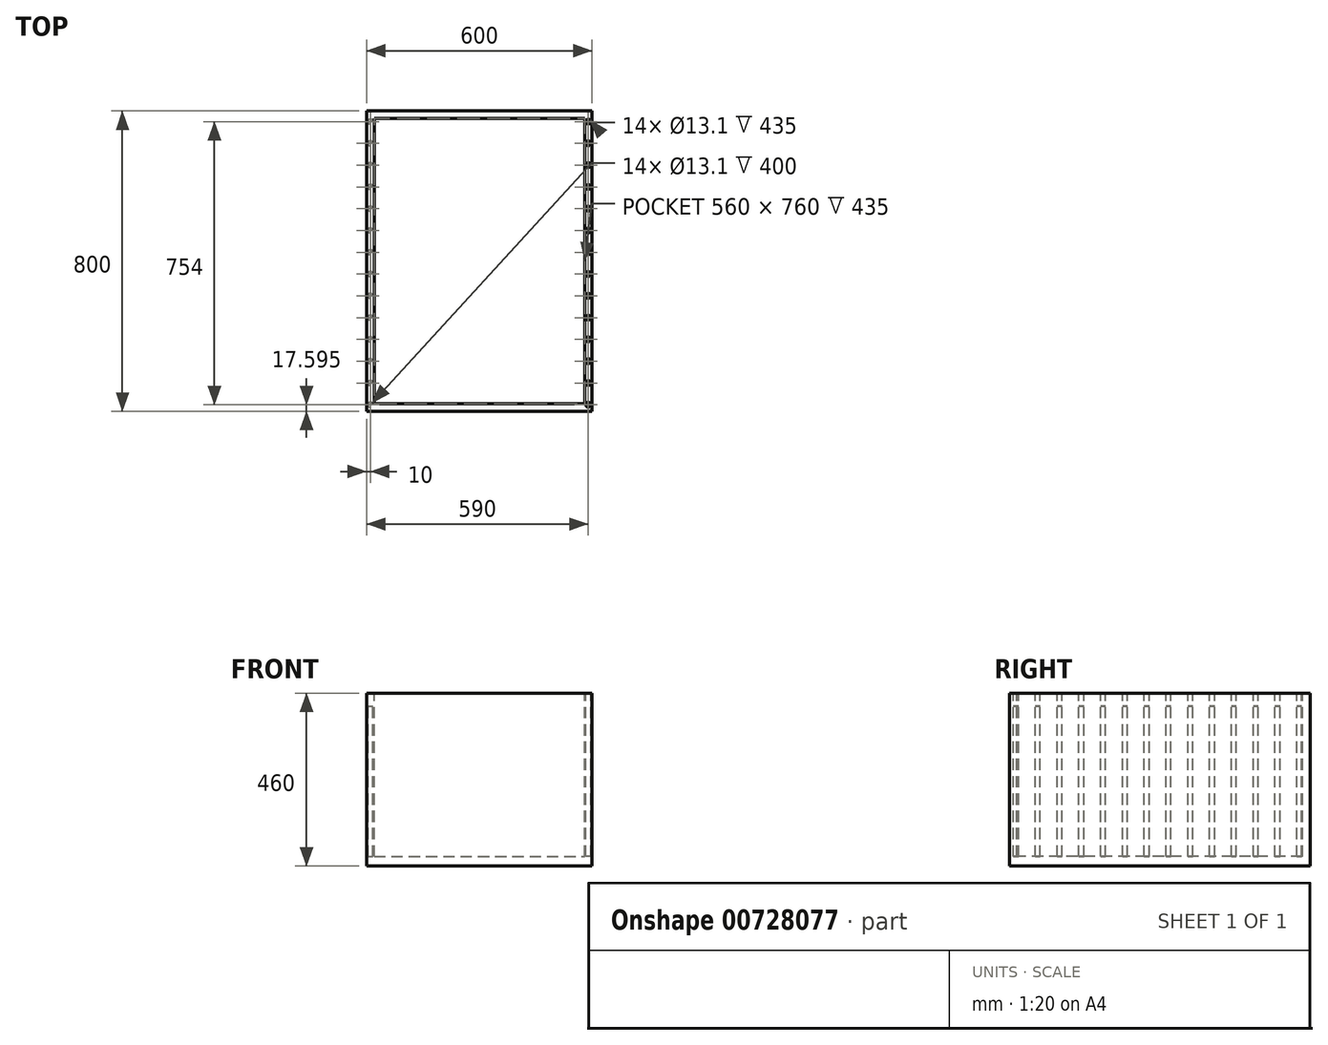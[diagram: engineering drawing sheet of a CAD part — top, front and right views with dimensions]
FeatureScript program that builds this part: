
annotation { "Feature Type Name" : "Feature", "Feature Type Description" : "" }
export const myFeature = defineFeature(function(context is Context, id is Id, definition is map)
    precondition{}
    {
        {
            var Q0;
            Q0=qCreatedBy(makeId("Top.planeOp"),FACE);
            var sketch = newSketch(context, id + "F0", { "sketchPlane" : qUnion([Q0])});
            skLineSegment(sketch, "E0.bottom", {"start": v(-307, 349) * mm, "end": v(293, 349) * mm});
            skLineSegment(sketch, "E0.top", {"start": v(-307, -451) * mm, "end": v(293, -451) * mm});
            skLineSegment(sketch, "E0.left", {"start": v(-307, 349) * mm, "end": v(-307, -451) * mm});
            skLineSegment(sketch, "E0.right", {"start": v(293, 349) * mm, "end": v(293, -451) * mm});
            skLineSegment(sketch, "E1.0", {"start": v(-287, 329) * mm, "end": v(273, 329) * mm});
            skLineSegment(sketch, "E1.1", {"start": v(-287, 329) * mm, "end": v(-287, -431) * mm});
            skLineSegment(sketch, "E1.2", {"start": v(-287, -431) * mm, "end": v(273, -431) * mm});
            skLineSegment(sketch, "E1.3", {"start": v(273, 329) * mm, "end": v(273, -431) * mm});
            skLineSegment(sketch, "E2", {"start": v(-307, -51) * mm, "end": v(-287, -51) * mm, "construction": true});
            skLineSegment(sketch, "E3", {"start": v(-287, -51) * mm, "end": v(-297, -51) * mm, "construction": true});
            skLineSegment(sketch, "E4", {"start": v(-297, -51) * mm, "end": v(-297, -27.4) * mm, "construction": true});
            skCircle(sketch, "E5", {"center": v(-297, -27.4) * mm, "radius": 6.55 * mm});
            skCircle(sketch, "E6.0.1.0", {"center": v(-297, 30.6) * mm, "radius": 6.55 * mm});
            skCircle(sketch, "E6.0.2.0", {"center": v(-297, 88.6) * mm, "radius": 6.55 * mm});
            skCircle(sketch, "E6.0.3.0", {"center": v(-297, 146.6) * mm, "radius": 6.55 * mm});
            skCircle(sketch, "E6.0.4.0", {"center": v(-297, 204.6) * mm, "radius": 6.55 * mm});
            skCircle(sketch, "E6.0.5.0", {"center": v(-297, 262.6) * mm, "radius": 6.55 * mm});
            skCircle(sketch, "E6.0.6.0", {"center": v(-297, 320.6) * mm, "radius": 6.55 * mm});
            skLineSegment(sketch, "E6.direction1", {"start": v(-297, -27.4) * mm, "end": v(-272, -27.4) * mm, "construction": true});
            skLineSegment(sketch, "E6.direction2", {"start": v(-297, -27.4) * mm, "end": v(-297, 30.6) * mm, "construction": true});
            skCircle(sketch, "E7.0.1.0", {"center": v(-297, -85.4) * mm, "radius": 6.55 * mm});
            skCircle(sketch, "E7.0.2.0", {"center": v(-297, -143.4) * mm, "radius": 6.55 * mm});
            skCircle(sketch, "E7.0.3.0", {"center": v(-297, -201.4) * mm, "radius": 6.55 * mm});
            skCircle(sketch, "E7.0.4.0", {"center": v(-297, -259.4) * mm, "radius": 6.55 * mm});
            skCircle(sketch, "E7.0.5.0", {"center": v(-297, -317.4) * mm, "radius": 6.55 * mm});
            skCircle(sketch, "E7.0.6.0", {"center": v(-297, -375.4) * mm, "radius": 6.55 * mm});
            skCircle(sketch, "E7.0.7.0", {"center": v(-297, -433.4) * mm, "radius": 6.55 * mm});
            skLineSegment(sketch, "E7.direction1", {"start": v(-297, -27.4) * mm, "end": v(-257, -27.4) * mm, "construction": true});
            skLineSegment(sketch, "E7.direction2", {"start": v(-297, -27.4) * mm, "end": v(-297, -85.4) * mm, "construction": true});
            skLineSegment(sketch, "E8", {"start": v(-7, 329) * mm, "end": v(-7, -431) * mm, "construction": true});
            skCircle(sketch, "E9.MirrorC", {"center": v(283, 320.6) * mm, "radius": 6.55 * mm});
            skCircle(sketch, "E10.MirrorC", {"center": v(283, 262.6) * mm, "radius": 6.55 * mm});
            skCircle(sketch, "E11.MirrorC", {"center": v(283, 204.6) * mm, "radius": 6.55 * mm});
            skCircle(sketch, "E12.MirrorC", {"center": v(283, 146.6) * mm, "radius": 6.55 * mm});
            skCircle(sketch, "E13.MirrorC", {"center": v(283, 88.6) * mm, "radius": 6.55 * mm});
            skCircle(sketch, "E14.MirrorC", {"center": v(283, 30.6) * mm, "radius": 6.55 * mm});
            skCircle(sketch, "E15.MirrorC", {"center": v(283, -27.4) * mm, "radius": 6.55 * mm});
            skCircle(sketch, "E16.MirrorC", {"center": v(283, -85.4) * mm, "radius": 6.55 * mm});
            skCircle(sketch, "E17.MirrorC", {"center": v(283, -143.4) * mm, "radius": 6.55 * mm});
            skCircle(sketch, "E18.MirrorC", {"center": v(283, -201.4) * mm, "radius": 6.55 * mm});
            skCircle(sketch, "E19.MirrorC", {"center": v(283, -259.4) * mm, "radius": 6.55 * mm});
            skCircle(sketch, "E20.MirrorC", {"center": v(283, -317.4) * mm, "radius": 6.55 * mm});
            skCircle(sketch, "E21.MirrorC", {"center": v(283, -375.4) * mm, "radius": 6.55 * mm});
            skCircle(sketch, "E22.MirrorC", {"center": v(283, -433.4) * mm, "radius": 6.55 * mm});
            skSolve(sketch);
        }
        {
            var Q0;
            Q0=makeQuery(id+"F0.imprint","IMPRINT",FACE,{"disambiguationData":[TD([[makeQuery(id+"F0.imprint","IMPRINT",EDGE,{"derivedFrom":sQuery(id+"F0.wireOp",EDGE,"E0.bottom")}),-1.0]])]});
            var Q1;
            Q1=makeQuery(id+"F0.imprint","IMPRINT",FACE,{"disambiguationData":[TD([[makeQuery(id+"F0.imprint","IMPRINT",EDGE,{"derivedFrom":sQuery(id+"F0.wireOp",EDGE,"E22.MirrorC")}),-1.0]])]});
            var Q2;
            Q2=makeQuery(id+"F0.imprint","IMPRINT",FACE,{"disambiguationData":[TD([[makeQuery(id+"F0.imprint","IMPRINT",EDGE,{"derivedFrom":sQuery(id+"F0.wireOp",EDGE,"E21.MirrorC")}),-1.0]])]});
            var Q3;
            Q3=makeQuery(id+"F0.imprint","IMPRINT",FACE,{"disambiguationData":[TD([[makeQuery(id+"F0.imprint","IMPRINT",EDGE,{"derivedFrom":sQuery(id+"F0.wireOp",EDGE,"E20.MirrorC")}),-1.0]])]});
            var Q4;
            Q4=makeQuery(id+"F0.imprint","IMPRINT",FACE,{"disambiguationData":[TD([[makeQuery(id+"F0.imprint","IMPRINT",EDGE,{"derivedFrom":sQuery(id+"F0.wireOp",EDGE,"E19.MirrorC")}),-1.0]])]});
            var Q5;
            Q5=makeQuery(id+"F0.imprint","IMPRINT",FACE,{"disambiguationData":[TD([[makeQuery(id+"F0.imprint","IMPRINT",EDGE,{"derivedFrom":sQuery(id+"F0.wireOp",EDGE,"E18.MirrorC")}),-1.0]])]});
            var Q6;
            Q6=makeQuery(id+"F0.imprint","IMPRINT",FACE,{"disambiguationData":[TD([[makeQuery(id+"F0.imprint","IMPRINT",EDGE,{"derivedFrom":sQuery(id+"F0.wireOp",EDGE,"E17.MirrorC")}),-1.0]])]});
            var Q7;
            Q7=makeQuery(id+"F0.imprint","IMPRINT",FACE,{"disambiguationData":[TD([[makeQuery(id+"F0.imprint","IMPRINT",EDGE,{"derivedFrom":sQuery(id+"F0.wireOp",EDGE,"E16.MirrorC")}),-1.0]])]});
            var Q8;
            Q8=makeQuery(id+"F0.imprint","IMPRINT",FACE,{"disambiguationData":[TD([[makeQuery(id+"F0.imprint","IMPRINT",EDGE,{"derivedFrom":sQuery(id+"F0.wireOp",EDGE,"E15.MirrorC")}),-1.0]])]});
            var Q9;
            Q9=makeQuery(id+"F0.imprint","IMPRINT",FACE,{"disambiguationData":[TD([[makeQuery(id+"F0.imprint","IMPRINT",EDGE,{"derivedFrom":sQuery(id+"F0.wireOp",EDGE,"E14.MirrorC")}),-1.0]])]});
            var Q10;
            Q10=makeQuery(id+"F0.imprint","IMPRINT",FACE,{"disambiguationData":[TD([[makeQuery(id+"F0.imprint","IMPRINT",EDGE,{"derivedFrom":sQuery(id+"F0.wireOp",EDGE,"E13.MirrorC")}),-1.0]])]});
            var Q11;
            Q11=makeQuery(id+"F0.imprint","IMPRINT",FACE,{"disambiguationData":[TD([[makeQuery(id+"F0.imprint","IMPRINT",EDGE,{"derivedFrom":sQuery(id+"F0.wireOp",EDGE,"E12.MirrorC")}),-1.0]])]});
            var Q12;
            Q12=makeQuery(id+"F0.imprint","IMPRINT",FACE,{"disambiguationData":[TD([[makeQuery(id+"F0.imprint","IMPRINT",EDGE,{"derivedFrom":sQuery(id+"F0.wireOp",EDGE,"E11.MirrorC")}),-1.0]])]});
            var Q13;
            Q13=makeQuery(id+"F0.imprint","IMPRINT",FACE,{"disambiguationData":[TD([[makeQuery(id+"F0.imprint","IMPRINT",EDGE,{"derivedFrom":sQuery(id+"F0.wireOp",EDGE,"E10.MirrorC")}),-1.0]])]});
            var Q14;
            Q14=makeQuery(id+"F0.imprint","IMPRINT",FACE,{"disambiguationData":[TD([[makeQuery(id+"F0.imprint","IMPRINT",EDGE,{"derivedFrom":sQuery(id+"F0.wireOp",EDGE,"E9.MirrorC")}),-1.0]])]});
            var Q15;
            Q15=makeQuery(id+"F0.imprint","IMPRINT",FACE,{"disambiguationData":[TD([[makeQuery(id+"F0.imprint","IMPRINT",EDGE,{"derivedFrom":sQuery(id+"F0.wireOp",EDGE,"E6.0.6.0")}),1.0]])]});
            var Q16;
            Q16=makeQuery(id+"F0.imprint","IMPRINT",FACE,{"disambiguationData":[TD([[makeQuery(id+"F0.imprint","IMPRINT",EDGE,{"derivedFrom":sQuery(id+"F0.wireOp",EDGE,"E6.0.5.0")}),1.0]])]});
            var Q17;
            Q17=makeQuery(id+"F0.imprint","IMPRINT",FACE,{"disambiguationData":[TD([[makeQuery(id+"F0.imprint","IMPRINT",EDGE,{"derivedFrom":sQuery(id+"F0.wireOp",EDGE,"E6.0.4.0")}),1.0]])]});
            var Q18;
            Q18=makeQuery(id+"F0.imprint","IMPRINT",FACE,{"disambiguationData":[TD([[makeQuery(id+"F0.imprint","IMPRINT",EDGE,{"derivedFrom":sQuery(id+"F0.wireOp",EDGE,"E6.0.3.0")}),1.0]])]});
            var Q19;
            Q19=makeQuery(id+"F0.imprint","IMPRINT",FACE,{"disambiguationData":[TD([[makeQuery(id+"F0.imprint","IMPRINT",EDGE,{"derivedFrom":sQuery(id+"F0.wireOp",EDGE,"E6.0.2.0")}),1.0]])]});
            var Q20;
            Q20=makeQuery(id+"F0.imprint","IMPRINT",FACE,{"disambiguationData":[TD([[makeQuery(id+"F0.imprint","IMPRINT",EDGE,{"derivedFrom":sQuery(id+"F0.wireOp",EDGE,"E6.0.1.0")}),1.0]])]});
            var Q21;
            Q21=makeQuery(id+"F0.imprint","IMPRINT",FACE,{"disambiguationData":[TD([[makeQuery(id+"F0.imprint","IMPRINT",EDGE,{"derivedFrom":sQuery(id+"F0.wireOp",EDGE,"E5")}),1.0]])]});
            var Q22;
            Q22=makeQuery(id+"F0.imprint","IMPRINT",FACE,{"disambiguationData":[TD([[makeQuery(id+"F0.imprint","IMPRINT",EDGE,{"derivedFrom":sQuery(id+"F0.wireOp",EDGE,"E7.0.1.0")}),1.0]])]});
            var Q23;
            Q23=makeQuery(id+"F0.imprint","IMPRINT",FACE,{"disambiguationData":[TD([[makeQuery(id+"F0.imprint","IMPRINT",EDGE,{"derivedFrom":sQuery(id+"F0.wireOp",EDGE,"E7.0.2.0")}),1.0]])]});
            var Q24;
            Q24=makeQuery(id+"F0.imprint","IMPRINT",FACE,{"disambiguationData":[TD([[makeQuery(id+"F0.imprint","IMPRINT",EDGE,{"derivedFrom":sQuery(id+"F0.wireOp",EDGE,"E7.0.3.0")}),1.0]])]});
            var Q25;
            Q25=makeQuery(id+"F0.imprint","IMPRINT",FACE,{"disambiguationData":[TD([[makeQuery(id+"F0.imprint","IMPRINT",EDGE,{"derivedFrom":sQuery(id+"F0.wireOp",EDGE,"E7.0.4.0")}),1.0]])]});
            var Q26;
            Q26=makeQuery(id+"F0.imprint","IMPRINT",FACE,{"disambiguationData":[TD([[makeQuery(id+"F0.imprint","IMPRINT",EDGE,{"derivedFrom":sQuery(id+"F0.wireOp",EDGE,"E7.0.5.0")}),1.0]])]});
            var Q27;
            Q27=makeQuery(id+"F0.imprint","IMPRINT",FACE,{"disambiguationData":[TD([[makeQuery(id+"F0.imprint","IMPRINT",EDGE,{"derivedFrom":sQuery(id+"F0.wireOp",EDGE,"E7.0.6.0")}),1.0]])]});
            var Q28;
            Q28=makeQuery(id+"F0.imprint","IMPRINT",FACE,{"disambiguationData":[TD([[makeQuery(id+"F0.imprint","IMPRINT",EDGE,{"derivedFrom":sQuery(id+"F0.wireOp",EDGE,"E7.0.7.0")}),1.0]])]});
            extrude(context, id + "F1", {"entities" : qUnion([Q0, Q1, Q2, Q3, Q4, Q5, Q6, Q7, Q8, Q9, Q10, Q11, Q12, Q13, Q14, Q15, Q16, Q17, Q18, Q19, Q20, Q21, Q22, Q23, Q24, Q25, Q26, Q27, Q28]), "oppositeDirection" : true, "depth" : 35 * mm});
        }
        {
            var Q0;
            Q0=makeQuery(id+"F1.opExtrude","CAP_FACE",FACE,{"disambiguationData":[OSD([sQuery(id+"F0.wireOp",EDGE,"E0.bottom"),sQuery(id+"F0.wireOp",EDGE,"E0.top"),sQuery(id+"F0.wireOp",EDGE,"E0.left"),sQuery(id+"F0.wireOp",EDGE,"E0.right"),sQuery(id+"F0.wireOp",EDGE,"E1.0"),sQuery(id+"F0.wireOp",EDGE,"E1.1"),sQuery(id+"F0.wireOp",EDGE,"E1.2"),sQuery(id+"F0.wireOp",EDGE,"E1.3")])],"isStart":false});
            var sketch = newSketch(context, id + "F2", { "sketchPlane" : qUnion([Q0])});
            skCircle(sketch, "E23.0", {"center": v(283, 85.4) * mm, "radius": 6.55 * mm});
            skCircle(sketch, "E23.1", {"center": v(283, -320.6) * mm, "radius": 6.55 * mm});
            skCircle(sketch, "E23.2", {"center": v(283, -204.6) * mm, "radius": 6.55 * mm});
            skCircle(sketch, "E23.3", {"center": v(283, -262.6) * mm, "radius": 6.55 * mm});
            skCircle(sketch, "E23.4", {"center": v(283, 143.4) * mm, "radius": 6.55 * mm});
            skCircle(sketch, "E23.5", {"center": v(283, 259.4) * mm, "radius": 6.55 * mm});
            skCircle(sketch, "E23.6", {"center": v(283, -146.6) * mm, "radius": 6.55 * mm});
            skCircle(sketch, "E23.7", {"center": v(283, 317.4) * mm, "radius": 6.55 * mm});
            skCircle(sketch, "E23.8", {"center": v(283, 201.4) * mm, "radius": 6.55 * mm});
            skCircle(sketch, "E23.9", {"center": v(283, -30.6) * mm, "radius": 6.55 * mm});
            skCircle(sketch, "E23.10", {"center": v(283, 27.4) * mm, "radius": 6.55 * mm});
            skCircle(sketch, "E23.11", {"center": v(283, 433.4) * mm, "radius": 6.55 * mm});
            skCircle(sketch, "E23.12", {"center": v(283, 375.4) * mm, "radius": 6.55 * mm});
            skCircle(sketch, "E23.13", {"center": v(283, -88.6) * mm, "radius": 6.55 * mm});
            skCircle(sketch, "E24.0", {"center": v(-297, -30.6) * mm, "radius": 6.55 * mm});
            skCircle(sketch, "E24.1", {"center": v(-297, 259.4) * mm, "radius": 6.55 * mm});
            skCircle(sketch, "E24.2", {"center": v(-297, -320.6) * mm, "radius": 6.55 * mm});
            skLineSegment(sketch, "E24.3", {"start": v(-297, 51) * mm, "end": v(-297, 27.4) * mm});
            skCircle(sketch, "E24.4", {"center": v(-297, -204.6) * mm, "radius": 6.55 * mm});
            skCircle(sketch, "E24.5", {"center": v(-297, -146.6) * mm, "radius": 6.55 * mm});
            skCircle(sketch, "E24.6", {"center": v(-297, 201.4) * mm, "radius": 6.55 * mm});
            skCircle(sketch, "E24.7", {"center": v(-297, 317.4) * mm, "radius": 6.55 * mm});
            skCircle(sketch, "E24.8", {"center": v(-297, 375.4) * mm, "radius": 6.55 * mm});
            skCircle(sketch, "E24.9", {"center": v(-297, -88.6) * mm, "radius": 6.55 * mm});
            skCircle(sketch, "E24.10", {"center": v(-297, 143.4) * mm, "radius": 6.55 * mm});
            skCircle(sketch, "E24.11", {"center": v(-297, 27.4) * mm, "radius": 6.55 * mm});
            skLineSegment(sketch, "E24.12", {"start": v(-297, 27.4) * mm, "end": v(-297, 85.4) * mm});
            skCircle(sketch, "E24.13", {"center": v(-297, -262.6) * mm, "radius": 6.55 * mm});
            skCircle(sketch, "E24.14", {"center": v(-297, 85.4) * mm, "radius": 6.55 * mm});
            skLineSegment(sketch, "E24.15", {"start": v(-297, 27.4) * mm, "end": v(-297, -30.6) * mm});
            skCircle(sketch, "E24.16", {"center": v(-297, 433.4) * mm, "radius": 6.55 * mm});
            skSolve(sketch);
        }
        {
            var Q0;
            Q0=makeQuery(id+"F2.imprint","IMPRINT",FACE,{"disambiguationData":[TD([[makeQuery(id+"F2.imprint","IMPRINT",EDGE,{"derivedFrom":sQuery(id+"F2.wireOp",EDGE,"E24.16")}),-1.0]])]});
            var Q1;
            Q1=makeQuery(id+"F2.imprint","IMPRINT",FACE,{"disambiguationData":[TD([[makeQuery(id+"F2.imprint","IMPRINT",EDGE,{"derivedFrom":sQuery(id+"F2.wireOp",EDGE,"E24.10")}),-1.0]])]});
            var Q2;
            Q2=makeQuery(id+"F2.imprint","IMPRINT",FACE,{"disambiguationData":[TD([[makeQuery(id+"F2.imprint","IMPRINT",EDGE,{"derivedFrom":sQuery(id+"F2.wireOp",EDGE,"E24.8")}),-1.0]])]});
            var Q3;
            Q3=makeQuery(id+"F2.imprint","IMPRINT",FACE,{"disambiguationData":[TD([[makeQuery(id+"F2.imprint","IMPRINT",EDGE,{"derivedFrom":sQuery(id+"F2.wireOp",EDGE,"E24.4")}),-1.0]])]});
            var Q4;
            {var subQ0=sQuery(id+"F2.wireOp",EDGE,"E24.12");var subQ1=sQuery(id+"F2.wireOp",EDGE,"E24.11");var subQ2=makeQuery(id+"F2.imprint","INTERSECT",VERTEX,{"derivedFrom":[subQ1,subQ0]});Q4=makeQuery(id+"F2.imprint","IMPRINT",FACE,{"disambiguationData":[TD([[makeQuery(id+"F2.imprint","IMPRINT",EDGE,{"disambiguationData":[TD([[subQ2,-1.0]])],"derivedFrom":subQ1}),-1.0]])]});}
            var Q5;
            Q5=makeQuery(id+"F2.imprint","IMPRINT",FACE,{"disambiguationData":[TD([[makeQuery(id+"F2.imprint","IMPRINT",EDGE,{"derivedFrom":sQuery(id+"F2.wireOp",EDGE,"E24.13")}),-1.0]])]});
            var Q6;
            Q6=makeQuery(id+"F2.imprint","IMPRINT",FACE,{"disambiguationData":[TD([[makeQuery(id+"F2.imprint","IMPRINT",EDGE,{"derivedFrom":sQuery(id+"F2.wireOp",EDGE,"E24.5")}),-1.0]])]});
            var Q7;
            Q7=makeQuery(id+"F2.imprint","IMPRINT",FACE,{"disambiguationData":[TD([[makeQuery(id+"F2.imprint","IMPRINT",EDGE,{"derivedFrom":sQuery(id+"F2.wireOp",EDGE,"E24.1")}),-1.0]])]});
            var Q8;
            Q8=makeQuery(id+"F2.imprint","IMPRINT",FACE,{"disambiguationData":[TD([[makeQuery(id+"F2.imprint","IMPRINT",EDGE,{"derivedFrom":sQuery(id+"F2.wireOp",EDGE,"E23.13")}),1.0]])]});
            var Q9;
            Q9=makeQuery(id+"F2.imprint","IMPRINT",FACE,{"disambiguationData":[TD([[makeQuery(id+"F2.imprint","IMPRINT",EDGE,{"derivedFrom":sQuery(id+"F2.wireOp",EDGE,"E24.0")}),-1.0]])]});
            var Q10;
            Q10=makeQuery(id+"F2.imprint","IMPRINT",FACE,{"disambiguationData":[TD([[makeQuery(id+"F2.imprint","IMPRINT",EDGE,{"derivedFrom":sQuery(id+"F2.wireOp",EDGE,"E23.0")}),1.0]])]});
            var Q11;
            Q11=makeQuery(id+"F2.imprint","IMPRINT",FACE,{"disambiguationData":[TD([[makeQuery(id+"F2.imprint","IMPRINT",EDGE,{"derivedFrom":sQuery(id+"F2.wireOp",EDGE,"E23.1")}),1.0]])]});
            var Q12;
            Q12=makeQuery(id+"F2.imprint","IMPRINT",FACE,{"disambiguationData":[TD([[makeQuery(id+"F2.imprint","IMPRINT",EDGE,{"derivedFrom":sQuery(id+"F2.wireOp",EDGE,"E23.2")}),1.0]])]});
            var Q13;
            Q13=makeQuery(id+"F2.imprint","IMPRINT",FACE,{"disambiguationData":[TD([[makeQuery(id+"F2.imprint","IMPRINT",EDGE,{"derivedFrom":sQuery(id+"F2.wireOp",EDGE,"E23.3")}),1.0]])]});
            var Q14;
            Q14=makeQuery(id+"F2.imprint","IMPRINT",FACE,{"disambiguationData":[TD([[makeQuery(id+"F2.imprint","IMPRINT",EDGE,{"derivedFrom":sQuery(id+"F2.wireOp",EDGE,"E23.4")}),1.0]])]});
            var Q15;
            Q15=makeQuery(id+"F2.imprint","IMPRINT",FACE,{"disambiguationData":[TD([[makeQuery(id+"F2.imprint","IMPRINT",EDGE,{"derivedFrom":sQuery(id+"F2.wireOp",EDGE,"E23.5")}),1.0]])]});
            var Q16;
            Q16=makeQuery(id+"F2.imprint","IMPRINT",FACE,{"disambiguationData":[TD([[makeQuery(id+"F2.imprint","IMPRINT",EDGE,{"derivedFrom":sQuery(id+"F2.wireOp",EDGE,"E23.6")}),1.0]])]});
            var Q17;
            Q17=makeQuery(id+"F2.imprint","IMPRINT",FACE,{"disambiguationData":[TD([[makeQuery(id+"F2.imprint","IMPRINT",EDGE,{"derivedFrom":sQuery(id+"F2.wireOp",EDGE,"E23.7")}),1.0]])]});
            var Q18;
            Q18=makeQuery(id+"F2.imprint","IMPRINT",FACE,{"disambiguationData":[TD([[makeQuery(id+"F2.imprint","IMPRINT",EDGE,{"derivedFrom":sQuery(id+"F2.wireOp",EDGE,"E23.8")}),1.0]])]});
            var Q19;
            Q19=makeQuery(id+"F2.imprint","IMPRINT",FACE,{"disambiguationData":[TD([[makeQuery(id+"F2.imprint","IMPRINT",EDGE,{"derivedFrom":sQuery(id+"F2.wireOp",EDGE,"E23.9")}),1.0]])]});
            var Q20;
            Q20=makeQuery(id+"F2.imprint","IMPRINT",FACE,{"disambiguationData":[TD([[makeQuery(id+"F2.imprint","IMPRINT",EDGE,{"derivedFrom":sQuery(id+"F2.wireOp",EDGE,"E23.10")}),1.0]])]});
            var Q21;
            Q21=makeQuery(id+"F2.imprint","IMPRINT",FACE,{"disambiguationData":[TD([[makeQuery(id+"F2.imprint","IMPRINT",EDGE,{"derivedFrom":sQuery(id+"F2.wireOp",EDGE,"E24.14")}),-1.0]])]});
            var Q22;
            Q22=makeQuery(id+"F2.imprint","IMPRINT",FACE,{"disambiguationData":[TD([[makeQuery(id+"F2.imprint","IMPRINT",EDGE,{"derivedFrom":sQuery(id+"F2.wireOp",EDGE,"E24.6")}),-1.0]])]});
            var Q23;
            Q23=makeQuery(id+"F2.imprint","IMPRINT",FACE,{"disambiguationData":[TD([[makeQuery(id+"F2.imprint","IMPRINT",EDGE,{"derivedFrom":sQuery(id+"F2.wireOp",EDGE,"E24.9")}),-1.0]])]});
            var Q24;
            Q24=makeQuery(id+"F2.imprint","IMPRINT",FACE,{"disambiguationData":[TD([[makeQuery(id+"F2.imprint","IMPRINT",EDGE,{"derivedFrom":sQuery(id+"F2.wireOp",EDGE,"E24.7")}),-1.0]])]});
            var Q25;
            Q25=makeQuery(id+"F2.imprint","IMPRINT",FACE,{"disambiguationData":[TD([[makeQuery(id+"F2.imprint","IMPRINT",EDGE,{"derivedFrom":sQuery(id+"F2.wireOp",EDGE,"E24.2")}),-1.0]])]});
            var Q26;
            {var subQ0=sQuery(id+"F2.wireOp",EDGE,"E24.12");var subQ1=sQuery(id+"F2.wireOp",EDGE,"E24.11");var subQ2=makeQuery(id+"F2.imprint","INTERSECT",VERTEX,{"derivedFrom":[subQ1,subQ0]});Q26=makeQuery(id+"F2.imprint","IMPRINT",FACE,{"disambiguationData":[TD([[makeQuery(id+"F2.imprint","IMPRINT",EDGE,{"disambiguationData":[TD([[subQ2,1.0]])],"derivedFrom":subQ1}),-1.0]])]});}
            var Q27;
            Q27=makeQuery(id+"F2.imprint","IMPRINT",FACE,{"disambiguationData":[TD([[makeQuery(id+"F2.imprint","IMPRINT",EDGE,{"derivedFrom":sQuery(id+"F2.wireOp",EDGE,"E23.11")}),1.0]])]});
            var Q28;
            Q28=makeQuery(id+"F2.imprint","IMPRINT",FACE,{"disambiguationData":[TD([[makeQuery(id+"F2.imprint","IMPRINT",EDGE,{"derivedFrom":sQuery(id+"F2.wireOp",EDGE,"E23.12")}),1.0]])]});
            var Q29;
            Q29=sQuery(id+"F2.wireOp",EDGE,"E24.15");
            var Q30;
            Q30=sQuery(id+"F2.wireOp",EDGE,"E24.14");
            var Q31;
            Q31=sQuery(id+"F2.wireOp",EDGE,"E23.13");
            var Q32;
            Q32=sQuery(id+"F2.wireOp",EDGE,"E23.8");
            var Q33;
            Q33=sQuery(id+"F2.wireOp",EDGE,"E24.8");
            var Q34;
            Q34=sQuery(id+"F2.wireOp",EDGE,"E24.4");
            var Q35;
            Q35=sQuery(id+"F2.wireOp",EDGE,"E24.12");
            var Q36;
            Q36=sQuery(id+"F2.wireOp",EDGE,"E24.13");
            var Q37;
            Q37=sQuery(id+"F2.wireOp",EDGE,"E24.9");
            var Q38;
            Q38=sQuery(id+"F2.wireOp",EDGE,"E24.6");
            var Q39;
            Q39=sQuery(id+"F2.wireOp",EDGE,"E24.2");
            var Q40;
            Q40=sQuery(id+"F2.wireOp",EDGE,"E24.10");
            var Q41;
            Q41=sQuery(id+"F2.wireOp",EDGE,"E24.16");
            var Q42;
            Q42=sQuery(id+"F2.wireOp",EDGE,"E24.7");
            var Q43;
            Q43=sQuery(id+"F2.wireOp",EDGE,"E24.3");
            var Q44;
            Q44=sQuery(id+"F2.wireOp",EDGE,"E24.1");
            var Q45;
            Q45=sQuery(id+"F2.wireOp",EDGE,"E23.0");
            var Q46;
            Q46=sQuery(id+"F2.wireOp",EDGE,"E23.1");
            var Q47;
            Q47=sQuery(id+"F2.wireOp",EDGE,"E23.2");
            var Q48;
            Q48=sQuery(id+"F2.wireOp",EDGE,"E23.3");
            var Q49;
            Q49=sQuery(id+"F2.wireOp",EDGE,"E23.4");
            var Q50;
            Q50=sQuery(id+"F2.wireOp",EDGE,"E23.5");
            var Q51;
            Q51=sQuery(id+"F2.wireOp",EDGE,"E23.6");
            var Q52;
            Q52=sQuery(id+"F2.wireOp",EDGE,"E23.7");
            var Q53;
            Q53=sQuery(id+"F2.wireOp",EDGE,"E23.9");
            var Q54;
            Q54=sQuery(id+"F2.wireOp",EDGE,"E23.10");
            var Q55;
            Q55=sQuery(id+"F2.wireOp",EDGE,"E23.12");
            var Q56;
            Q56=sQuery(id+"F2.wireOp",EDGE,"E24.5");
            var Q57;
            Q57=sQuery(id+"F2.wireOp",EDGE,"E24.0");
            var Q58;
            Q58=sQuery(id+"F2.wireOp",EDGE,"E24.11");
            var Q59;
            Q59=sQuery(id+"F2.wireOp",EDGE,"E23.11");
            extrude(context, id + "F3", {"entities" : qUnion([Q0, Q1, Q2, Q3, Q4, Q5, Q6, Q7, Q8, Q9, Q10, Q11, Q12, Q13, Q14, Q15, Q16, Q17, Q18, Q19, Q20, Q21, Q22, Q23, Q24, Q25, Q26, Q27, Q28]), "operationType" : NewBodyOperationType.ADD, "surfaceEntities" : qUnion([Q29, Q30, Q31, Q32, Q33, Q34, Q35, Q36, Q37, Q38, Q39, Q40, Q41, Q42, Q43, Q44, Q45, Q46, Q47, Q48, Q49, Q50, Q51, Q52, Q53, Q54, Q55, Q56, Q57, Q58, Q59]), "depth" : 400 * mm});
        }
        {
            var Q0;
            Q0=makeQuery(id+"F3.opExtrude","CAP_FACE",FACE,{"disambiguationData":[OSD([sQuery(id+"F2.wireOp",EDGE,"E24.16")])],"isStart":false});
            var sketch = newSketch(context, id + "F4", { "sketchPlane" : qUnion([Q0])});
            skLineSegment(sketch, "E25.0", {"start": v(-307, 451) * mm, "end": v(293, 451) * mm});
            skLineSegment(sketch, "E26.0", {"start": v(-307, -349) * mm, "end": v(-307, 451) * mm});
            skLineSegment(sketch, "E27.0", {"start": v(-307, -349) * mm, "end": v(293, -349) * mm});
            skLineSegment(sketch, "E28.0", {"start": v(293, -349) * mm, "end": v(293, 451) * mm});
            skSolve(sketch);
        }
        {
            var Q0;
            Q0=qSketchRegion(id+"F4",true);
            extrude(context, id + "F5", {"entities" : qUnion([Q0]), "operationType" : NewBodyOperationType.ADD, "depth" : 25 * mm});
        }
    });
